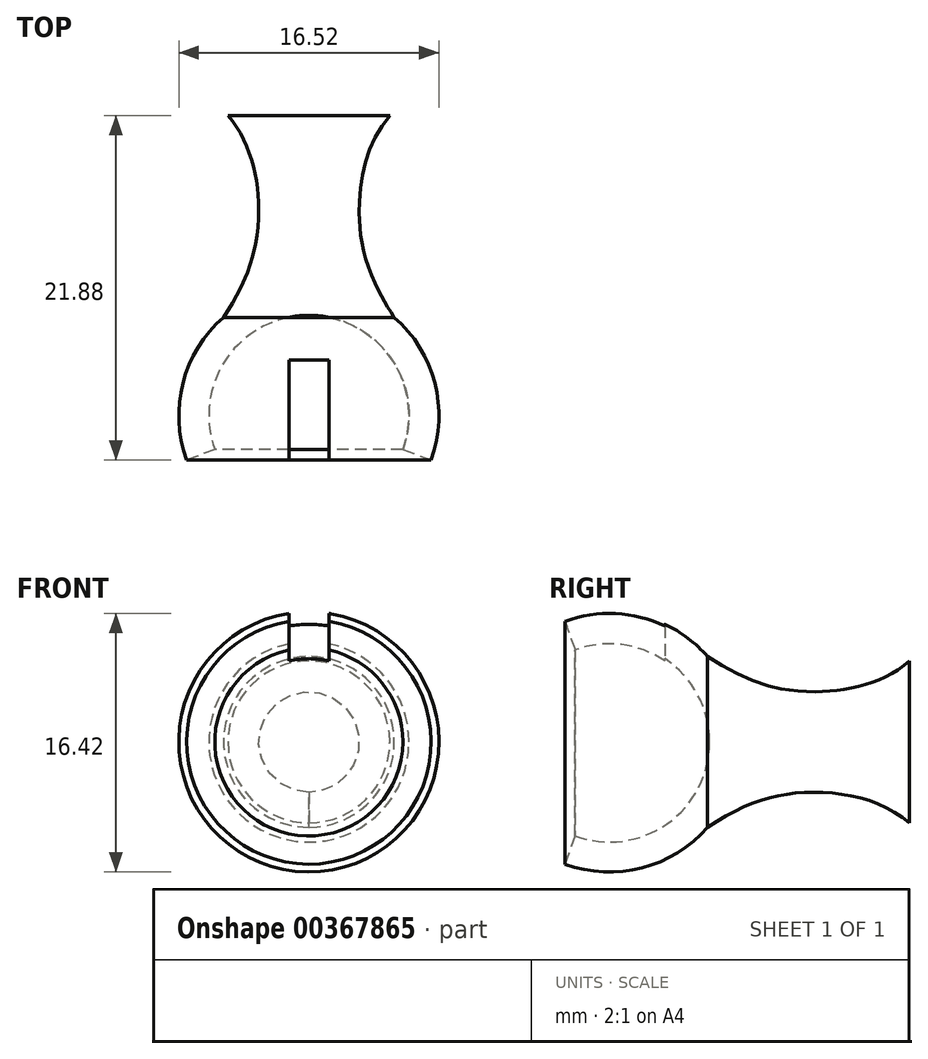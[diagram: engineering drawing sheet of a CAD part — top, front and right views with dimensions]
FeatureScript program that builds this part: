
annotation { "Feature Type Name" : "Feature", "Feature Type Description" : "" }
export const myFeature = defineFeature(function(context is Context, id is Id, definition is map)
    precondition{}
    {
        {
            var Q0;
            Q0=qCreatedBy(makeId("Top.planeOp"),FACE);
            var sketch = newSketch(context, id + "F0", { "sketchPlane" : qUnion([Q0])});
            skCircle(sketch, "E0", {"center": v(0, 0) * mm, "radius": 12.71 * mm});
            skCircle(sketch, "E1.0", {"center": v(0, 0) * mm, "radius": 16.52 * mm});
            skLineSegment(sketch, "E2", {"start": v(0, 0) * mm, "end": v(15.53, -5.65) * mm});
            skLineSegment(sketch, "E3.MirrorCS", {"start": v(0, 0) * mm, "end": v(-15.53, -5.65) * mm});
            skLineSegment(sketch, "E4", {"start": v(0, 0) * mm, "end": v(0, 38.1) * mm});
            skFitSpline(sketch, "E5", {"points": [v(10.84, 12.47) * mm, v(6.38, 25.5) * mm, v(10.28, 38.1) * mm], "startDerivative": vector(-18.2, 27.3) * mm, "endDerivative": vector(17.6, 19.95) * mm});
            skLineSegment(sketch, "E6", {"start": v(0, 38.1) * mm, "end": v(10.28, 38.1) * mm});
            skSolve(sketch);
        }
        {
            var Q0;
            {var subQ0=sQuery(id+"F0.wireOp",EDGE,"E5");Q0=makeQuery(id+"F0.imprint","IMPRINT",FACE,{"disambiguationData":[TD([[makeQuery(id+"F0.imprint","IMPRINT",EDGE,{"derivedFrom":subQ0}),1.0]])]});}
            var Q1;
            {var subQ4=sQuery(id+"F0.wireOp",EDGE,"E0");var subQ6=sQuery(id+"F0.wireOp",EDGE,"E4");var subQ8=makeQuery(id+"F0.imprint","INTERSECT",VERTEX,{"derivedFrom":[subQ4,subQ6]});Q1=makeQuery(id+"F0.imprint","IMPRINT",FACE,{"disambiguationData":[TD([[makeQuery(id+"F0.imprint","IMPRINT",EDGE,{"disambiguationData":[TD([[subQ8,1.0]])],"derivedFrom":subQ4}),-1.0]])]});}
            var Q2;
            Q2=sQuery(id+"F0.wireOp",EDGE,"E4");
            revolve(context, id + "F1", {"entities" : qUnion([Q0, Q1]), "axis" : qUnion([Q2]), "revolveType" : RevolveType.FULL});
        }
        {
            var Q0;
            Q0=qCreatedBy(makeId("Top.planeOp"),FACE);
            var sketch = newSketch(context, id + "F2", { "sketchPlane" : qUnion([Q0])});
            skLineSegment(sketch, "E7.bottom", {"start": v(0, -8.37) * mm, "end": v(2.54, -8.37) * mm});
            skLineSegment(sketch, "E7.top", {"start": v(0, 7.05) * mm, "end": v(2.54, 7.05) * mm});
            skLineSegment(sketch, "E7.left", {"start": v(0, -8.37) * mm, "end": v(0, 7.05) * mm});
            skLineSegment(sketch, "E7.right", {"start": v(2.54, -8.37) * mm, "end": v(2.54, 7.05) * mm});
            skLineSegment(sketch, "E8.MirrorCS", {"start": v(0, 7.05) * mm, "end": v(-2.54, 7.05) * mm});
            skLineSegment(sketch, "E9.MirrorCS", {"start": v(-2.54, -8.37) * mm, "end": v(-2.54, 7.05) * mm});
            skLineSegment(sketch, "E10.MirrorCS", {"start": v(0, -8.37) * mm, "end": v(-2.54, -8.37) * mm});
            skSolve(sketch);
        }
        {
            var Q0;
            Q0 = qSketchRegion(id + "F2", true);
            extrude(context, id + "F3", {"entities" : qUnion([Q0]), "operationType" : NewBodyOperationType.REMOVE, "depth" : 25.4 * mm});
        }
        {
            var Q0;
            Q0=makeQuery(id+"F1.opRevolve","SWEPT_BODY",BODY,{"disambiguationData":[OSD([sQuery(id+"F0.wireOp",EDGE,"E0"),sQuery(id+"F0.wireOp",EDGE,"E1.0"),sQuery(id+"F0.wireOp",EDGE,"E2"),sQuery(id+"F0.wireOp",EDGE,"E4"),sQuery(id+"F0.wireOp",EDGE,"E5"),sQuery(id+"F0.wireOp",EDGE,"E6")])]});
            var Q1;
            Q1=qCreatedBy(makeId("Origin.pointOp"),VERTEX);
            transform(context, id + "F4", {"entities" : qUnion([Q0]), "transformType" : TransformType.SCALE_UNIFORMLY, "scale" : .5, "scalePoint" : qUnion([Q1]), "makeCopy" : false});
        }
    });
